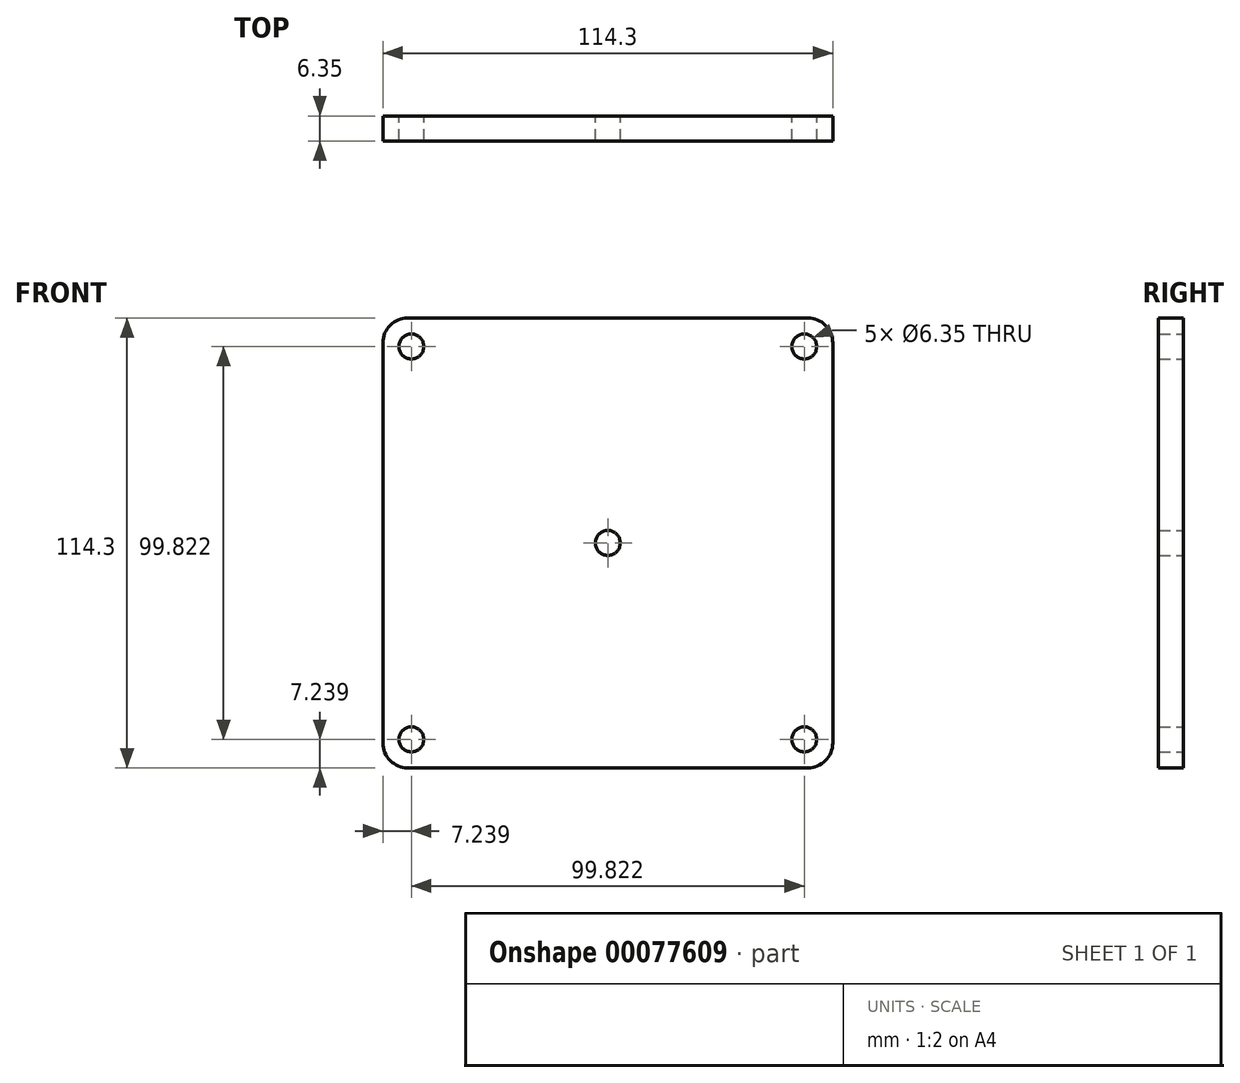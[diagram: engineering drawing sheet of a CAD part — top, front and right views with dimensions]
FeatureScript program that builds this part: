
annotation { "Feature Type Name" : "Feature", "Feature Type Description" : "" }
export const myFeature = defineFeature(function(context is Context, id is Id, definition is map)
    precondition{}
    {
        {
            var Q0;
            Q0=qCreatedBy(makeId("Front.planeOp"),FACE);
            var sketch = newSketch(context, id + "F0", { "sketchPlane" : qUnion([Q0])});
            skLineSegment(sketch, "E0.bottom", {"start": v(-50.8, 57.15) * mm, "end": v(50.8, 57.15) * mm});
            skLineSegment(sketch, "E0.top", {"start": v(-50.8, -57.15) * mm, "end": v(50.8, -57.15) * mm});
            skLineSegment(sketch, "E0.left", {"start": v(-57.15, 50.8) * mm, "end": v(-57.15, -50.8) * mm});
            skLineSegment(sketch, "E0.right", {"start": v(57.15, 50.8) * mm, "end": v(57.15, -50.8) * mm});
            skCircle(sketch, "E1", {"center": v(49.91, 49.91) * mm, "radius": 3.18 * mm});
            skCircle(sketch, "E2", {"center": v(49.91, -49.91) * mm, "radius": 3.18 * mm});
            skCircle(sketch, "E3.MirrorC", {"center": v(-49.91, 49.91) * mm, "radius": 3.18 * mm});
            skCircle(sketch, "E4.MirrorC", {"center": v(-49.91, -49.91) * mm, "radius": 3.18 * mm});
            skCircle(sketch, "E5", {"center": v(0, 0) * mm, "radius": 3.18 * mm});
            skPoint(sketch, "E6.visualSharp", {"position": v(-57.15, 57.15) * mm});
            skArc(sketch, "E6.filletArc", {"start": v(-50.8, 57.15) * mm, "mid": v(-55.3, 55.3) * mm, "end": v(-57.15, 50.8) * mm});
            skPoint(sketch, "E7.visualSharp", {"position": v(-57.15, -57.15) * mm});
            skArc(sketch, "E7.filletArc", {"start": v(-57.15, -50.8) * mm, "mid": v(-55.3, -55.3) * mm, "end": v(-50.8, -57.15) * mm});
            skPoint(sketch, "E8.visualSharp", {"position": v(57.15, -57.15) * mm});
            skArc(sketch, "E8.filletArc", {"start": v(50.8, -57.15) * mm, "mid": v(55.3, -55.3) * mm, "end": v(57.15, -50.8) * mm});
            skPoint(sketch, "E9.visualSharp", {"position": v(57.15, 57.15) * mm});
            skArc(sketch, "E9.filletArc", {"start": v(57.15, 50.8) * mm, "mid": v(55.3, 55.3) * mm, "end": v(50.8, 57.15) * mm});
            skSolve(sketch);
        }
        {
            var Q0;
            Q0 = qSketchRegion(id + "F0", true);
            extrude(context, id + "F1", {"entities" : qUnion([Q0]), "depth" : 6.35 * mm});
        }
    });
